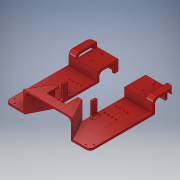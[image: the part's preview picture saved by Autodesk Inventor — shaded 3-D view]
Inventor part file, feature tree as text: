
AUTODESK INVENTOR PART (.ipt)
format: ipt  version: 2019 (Build 230136000, 136)  size: 485,888 bytes
history: native  units: in
note: dims shown in document units (in); Inventor stores cm internally (conversion verified against a paired STEP export)
features: extrude x18, sketch x17, fillet x3, mirror x2
ambient origin geometry x8: Origin, YZ Plane, XZ Plane, XY Plane, X Axis, Y Axis, Z Axis, Center Point
bodies: Solid1 (feature_tree)
feature tree (40):
  extrude  "Extrusion1"  Depth=2.17in
  extrude  "Extrusion2"  Depth=2.953in
  extrude  "Extrusion3"  Depth=0.1969in TaperAngle=0.0deg
  extrude  "Extrusion4"  Depth=0.1969in
  extrude  "Extrusion5"  Depth=2.25in
  extrude  "Extrusion6"  Depth=0.4134in TaperAngle=0.0deg
  extrude  "Extrusion7"  Depth=0.1969in
  extrude  "Extrusion8"  Depth=0.1969in
  extrude  "Extrusion9"  Depth=1.68in
  extrude  "Extrusion10"  Depth=0.5315in
  extrude  "Extrusion11"  Depth=0.1575in
  extrude  "Extrusion12"  Depth=1.0in TaperAngle=0.0deg
  extrude  "Extrusion13"  Depth=0.1969in
  mirror  "Mirror1"
  fillet  "Fillet4"  Radius=0.886in
  fillet  "Fillet5"  Radius=2.7638in
  extrude  "Extrusion14"  Depth=0.7874in
  extrude  "Extrusion15"  Depth=1.5748in
  mirror  "Mirror2"
  sketch  "Sketch18"  dims[d41=0.2362in d42=0.6102in]
  extrude  "Extrusion16"  Depth=0.6102in
  extrude  "Extrusion17"  Depth=0.3937in
  extrude  "Extrusion18"  Depth=0.3937in
  fillet  "Fillet6"  Radius=0.1378in
  sketch  "Sketch1"  dims[d0=1.422in d1=2.17in]
  sketch  "Sketch3"  dims[d2=1.422in d3=2.953in]
  sketch  "Sketch4"  dims[d4=6.75in d5=0.1969in d6=0.0in]
  sketch  "Sketch5"  dims[d7=2.953in d8=0.1969in]
  sketch  "Sketch6"  dims[d9=1.2992in d10=0.0in d11=2.25in]
  sketch  "Sketch8"  dims[d12=0.1969in d13=0.4134in d14=0.0in]
  sketch  "Sketch9"  dims[d15=0.1969in d16=0.1969in]
  sketch  "Sketch10"  dims[d17=2.0in d18=0.0in d19=0.1969in]
  sketch  "Sketch11"  dims[d20=0.4134in d21=0.0in d22=1.68in]
  sketch  "Sketch12"  dims[d23=0.9843in d24=0.5315in]
  sketch  "Sketch13"  dims[d25=1.063in d26=0.1575in]
  sketch  "Sketch14"  dims[d27=0.1575in d28=1.0in d29=0.0in]
  sketch  "Sketch15"  dims[d32=2.25in d33=0.1969in d34=0.886in d35=0.0in d36=2.7638in]
  sketch  "Sketch16"  dims[d37=4.0787in d38=0.7874in]
  sketch  "Sketch17"  dims[d39=1.6142in d40=1.5748in]
  sketch  "Sketch19"  dims[d43=0.1378in d44=0.2362in d45=0.6102in d46=0.1378in d47=1.5748in d49=0.3937in d50=0.3937in d52=1.0in d54=0.886in d55=0.0in d56=0.4528in d57=0.4528in d58=0.9055in d59=0.2953in d60=135.0deg d61=0.5906in d62=0.1181in d63=0.1181in d64=0.1969in d65=0.0in d66=0.1969in d67=5.25in d68=0.1969in d69=0.5in d70=1.45in d71=0.0in d72=0.25in d73=0.1969in d74=0.1575in d75=0.3937in d76=0.0in d77=0.1969in d78=0.2362in d79=0.0in d80=0.1181in d81=0.1575in d82=0.1575in d83=0.2362in d84=0.0in d88=0.3937in d89=0.1969in d94=1.9685in d96=1.9685in d97=0.0in d98=1.9685in d99=0.3937in d100=0.0in d102=7.874in d103=90.0deg d104=0.1575in d105=180.0deg d106=0.1575in d107=90.0deg d108=1.9685in d109=0.0in d110=0.1575in d111=1.9685in d112=0.0in d113=1.9685in d114=0.0in d115=7.874in d116=90.0deg d117=0.9843in d118=1.9685in d119=1.9685in d120=0.0in d121=0.3937in]
